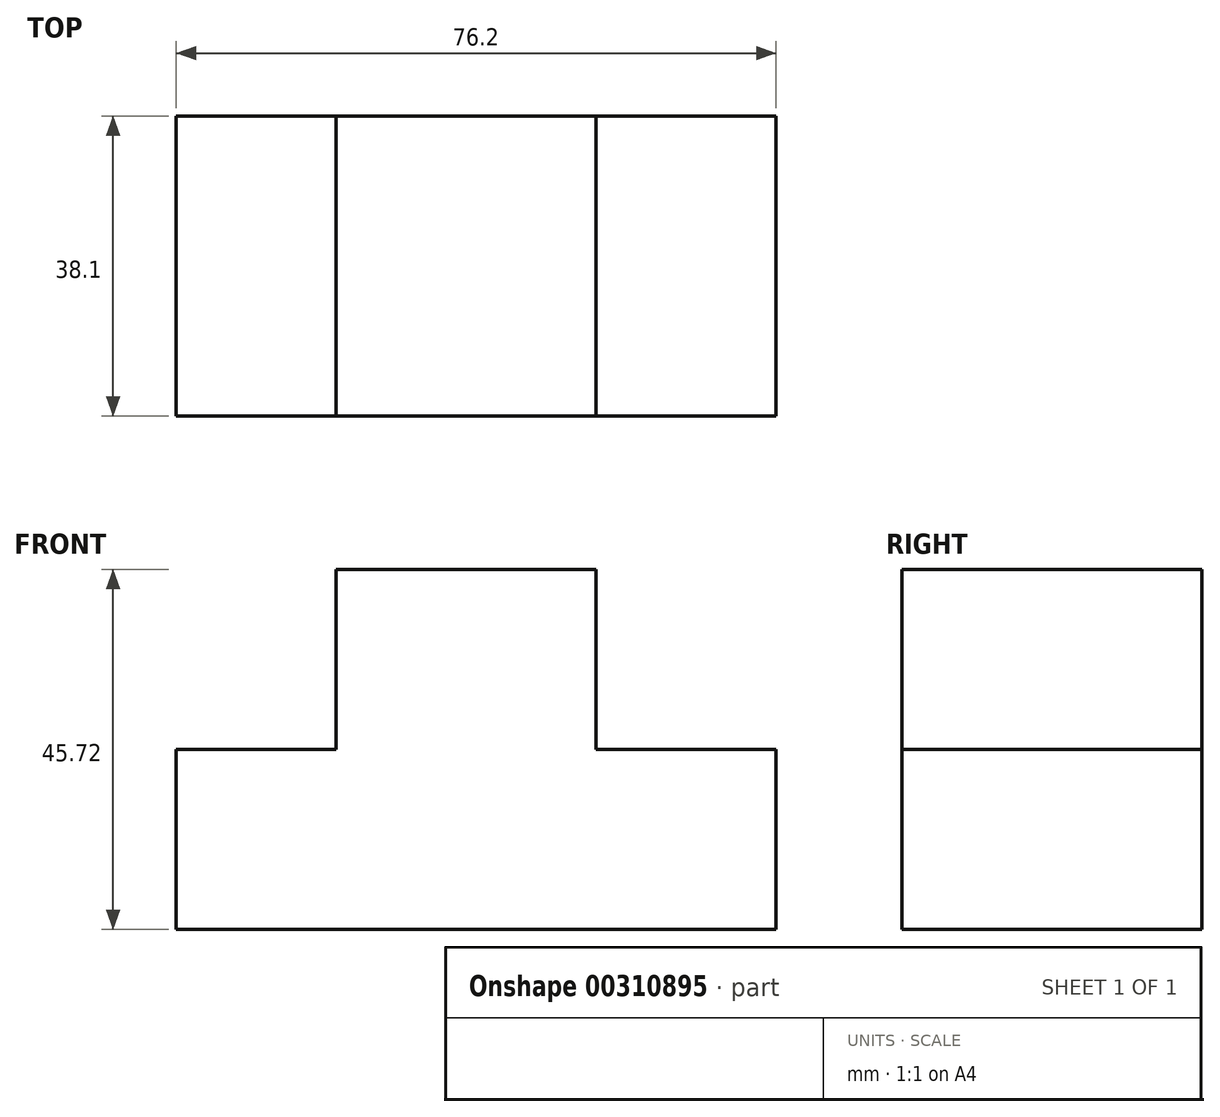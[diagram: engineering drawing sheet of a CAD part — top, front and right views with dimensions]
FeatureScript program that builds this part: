
annotation { "Feature Type Name" : "Feature", "Feature Type Description" : "" }
export const myFeature = defineFeature(function(context is Context, id is Id, definition is map)
    precondition{}
    {
        {
            var Q0;
            Q0=qCreatedBy(makeId("Front.planeOp"),FACE);
            var sketch = newSketch(context, id + "F0", { "sketchPlane" : qUnion([Q0])});
            skLineSegment(sketch, "E0", {"start": v(-39.5, -38.32) * mm, "end": v(36.7, -38.32) * mm});
            skLineSegment(sketch, "E1", {"start": v(36.7, -38.32) * mm, "end": v(36.7, -15.46) * mm});
            skLineSegment(sketch, "E2", {"start": v(13.85, -15.46) * mm, "end": v(36.7, -15.46) * mm});
            skLineSegment(sketch, "E3", {"start": v(13.85, -15.46) * mm, "end": v(13.85, 7.4) * mm});
            skLineSegment(sketch, "E4", {"start": v(13.85, 7.4) * mm, "end": v(-19.17, 7.4) * mm});
            skLineSegment(sketch, "E5", {"start": v(-19.17, -15.46) * mm, "end": v(-19.17, 7.4) * mm});
            skLineSegment(sketch, "E6", {"start": v(-39.5, -38.32) * mm, "end": v(-39.5, -15.46) * mm});
            skLineSegment(sketch, "E7", {"start": v(-39.5, -15.46) * mm, "end": v(-19.17, -15.46) * mm});
            skSolve(sketch);
        }
        {
            var Q0;
            Q0 = qSketchRegion(id + "F0", true);
            extrude(context, id + "F1", {"entities" : qUnion([Q0]), "depth" : 38.1 * mm});
        }
    });
